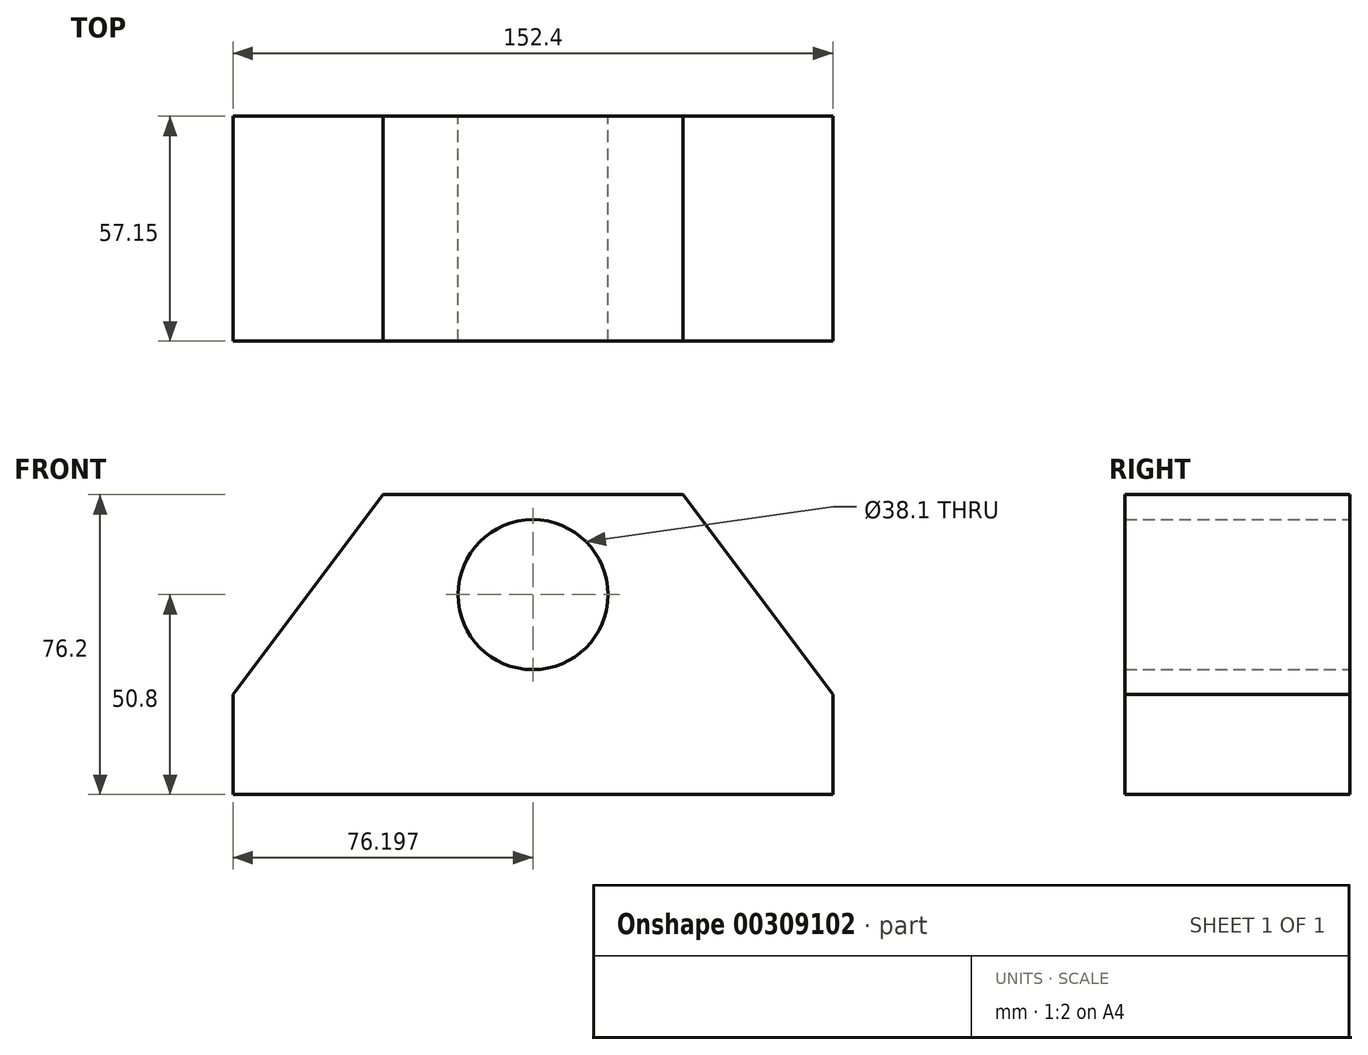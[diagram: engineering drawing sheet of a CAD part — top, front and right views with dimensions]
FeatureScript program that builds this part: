
annotation { "Feature Type Name" : "Feature", "Feature Type Description" : "" }
export const myFeature = defineFeature(function(context is Context, id is Id, definition is map)
    precondition{}
    {
        {
            var Q0;
            Q0=qCreatedBy(makeId("Front.planeOp"),FACE);
            var sketch = newSketch(context, id + "F0", { "sketchPlane" : qUnion([Q0])});
            skLineSegment(sketch, "E0.bottom", {"start": v(-56.78, -50.8) * mm, "end": v(95.62, -50.8) * mm});
            skLineSegment(sketch, "E0.left", {"start": v(-56.78, -50.8) * mm, "end": v(-56.78, -25.4) * mm});
            skLineSegment(sketch, "E0.right", {"start": v(95.62, -50.8) * mm, "end": v(95.62, -25.4) * mm});
            skLineSegment(sketch, "E1", {"start": v(-56.78, -25.4) * mm, "end": v(-18.68, 25.4) * mm});
            skLineSegment(sketch, "E2", {"start": v(-18.68, 25.4) * mm, "end": v(57.52, 25.4) * mm});
            skLineSegment(sketch, "E3", {"start": v(57.52, 25.4) * mm, "end": v(95.62, -25.4) * mm});
            skCircle(sketch, "E4", {"center": v(19.42, 0) * mm, "radius": 19.05 * mm});
            skSolve(sketch);
        }
        {
            var Q0;
            Q0 = qSketchRegion(id + "F0", true);
            extrude(context, id + "F1", {"entities" : qUnion([Q0]), "depth" : 57.15 * mm});
        }
    });
